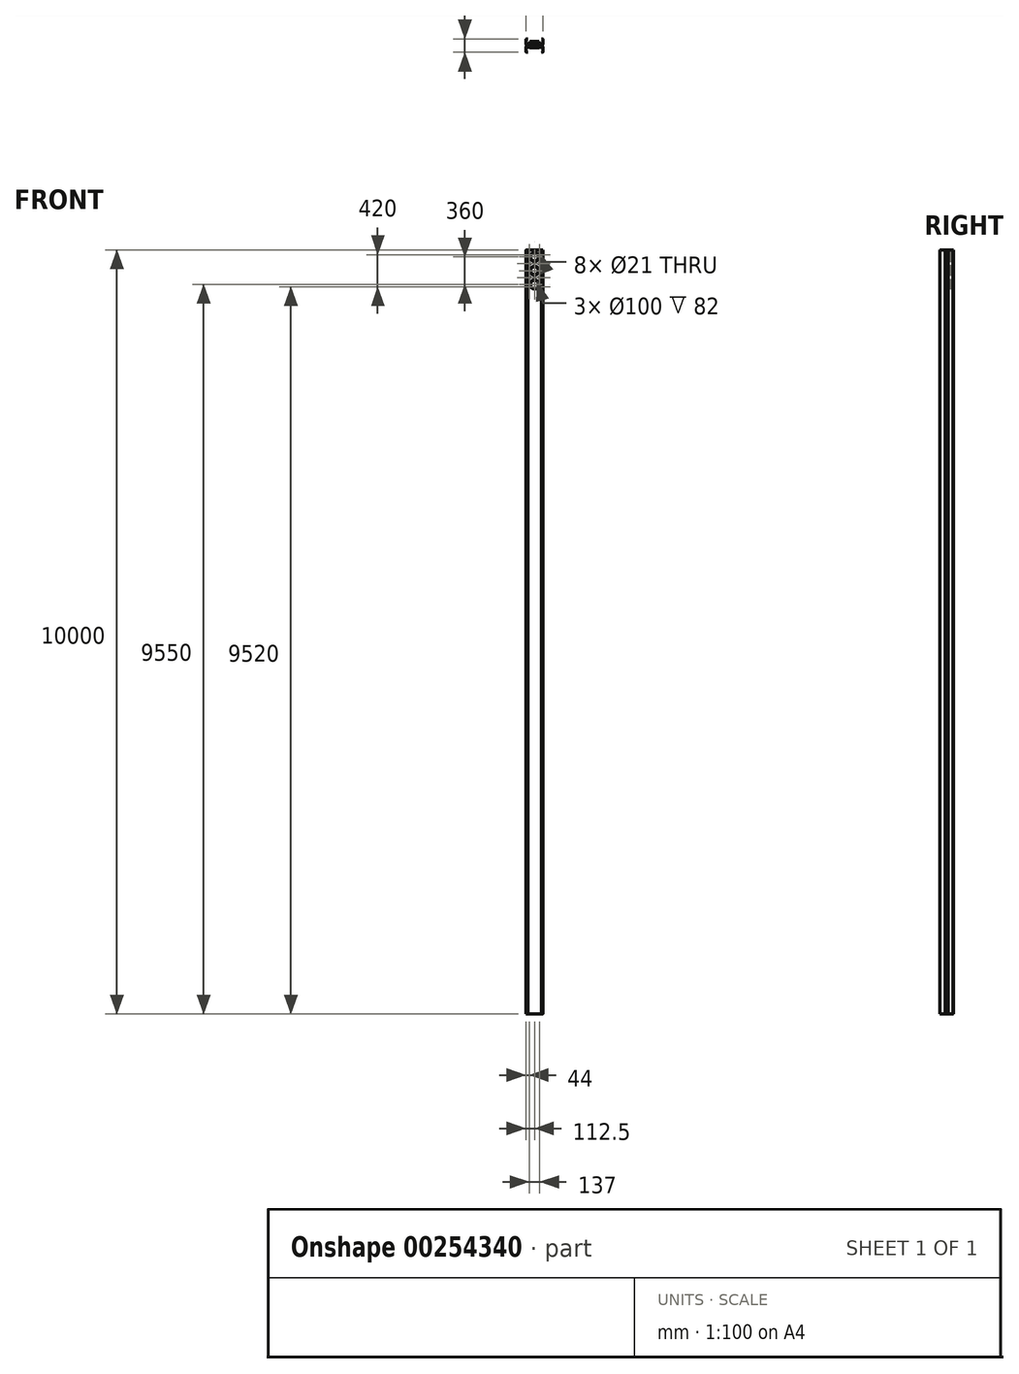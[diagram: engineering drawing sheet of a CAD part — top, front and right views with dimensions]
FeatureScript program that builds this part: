
annotation { "Feature Type Name" : "Feature", "Feature Type Description" : "" }
export const myFeature = defineFeature(function(context is Context, id is Id, definition is map)
    precondition{}
    {
        {
            var Q0;
            Q0=qCreatedBy(makeId("Top.planeOp"),FACE);
            var sketch = newSketch(context, id + "F0", { "sketchPlane" : qUnion([Q0])});
            skLineSegment(sketch, "E0.bottom", {"start": v(-107.5, 92.78) * mm, "end": v(-88.5, 92.78) * mm});
            skLineSegment(sketch, "E0.top", {"start": v(-107.5, -82.22) * mm, "end": v(-88.5, -82.22) * mm});
            skLineSegment(sketch, "E0.left", {"start": v(-112.5, 87.78) * mm, "end": v(-112.5, 26.84) * mm});
            skLineSegment(sketch, "E0.right", {"start": v(112.5, -18.27) * mm, "end": v(112.5, -77.22) * mm});
            skLineSegment(sketch, "E1.bottom", {"start": v(-104, 89.28) * mm, "end": v(-88.5, 89.28) * mm});
            skLineSegment(sketch, "E1.top", {"start": v(-104, 27.78) * mm, "end": v(104, 27.78) * mm});
            skLineSegment(sketch, "E1.left", {"start": v(-109, 84.28) * mm, "end": v(-109, 32.78) * mm});
            skLineSegment(sketch, "E1.right", {"start": v(109, 84.28) * mm, "end": v(109, 32.78) * mm});
            skLineSegment(sketch, "E2.bottom", {"start": v(-104, -17.22) * mm, "end": v(104, -17.22) * mm});
            skLineSegment(sketch, "E2.top", {"start": v(-104, -78.72) * mm, "end": v(-88.5, -78.72) * mm});
            skLineSegment(sketch, "E2.left", {"start": v(-109, -22.22) * mm, "end": v(-109, -73.72) * mm});
            skLineSegment(sketch, "E2.right", {"start": v(109, -22.22) * mm, "end": v(109, -73.72) * mm});
            skLineSegment(sketch, "E3.left", {"start": v(-88.5, 92.78) * mm, "end": v(-88.5, 89.28) * mm});
            skLineSegment(sketch, "E3.right", {"start": v(88.5, 92.78) * mm, "end": v(88.5, 89.28) * mm});
            skLineSegment(sketch, "E4.trimOffspring", {"start": v(-88.5, -78.72) * mm, "end": v(-88.5, -82.22) * mm});
            skLineSegment(sketch, "E5.trimOffspring", {"start": v(88.5, -78.72) * mm, "end": v(88.5, -82.22) * mm});
            skLineSegment(sketch, "E6.trimOffspring", {"start": v(88.5, -82.22) * mm, "end": v(107.5, -82.22) * mm});
            skLineSegment(sketch, "E7.trimOffspring", {"start": v(88.5, -78.72) * mm, "end": v(104, -78.72) * mm});
            skLineSegment(sketch, "E8.trimOffspring", {"start": v(88.5, 89.28) * mm, "end": v(104, 89.28) * mm});
            skLineSegment(sketch, "E9.trimOffspring", {"start": v(88.5, 92.78) * mm, "end": v(107.5, 92.78) * mm});
            skPoint(sketch, "E10.visualSharp", {"position": v(-109, 89.28) * mm});
            skArc(sketch, "E10.filletArc", {"start": v(-104, 89.28) * mm, "mid": v(-107.54, 87.81) * mm, "end": v(-109, 84.28) * mm});
            skPoint(sketch, "E11.visualSharp", {"position": v(109, 89.28) * mm});
            skArc(sketch, "E11.filletArc", {"start": v(109, 84.28) * mm, "mid": v(107.54, 87.81) * mm, "end": v(104, 89.28) * mm});
            skPoint(sketch, "E12.visualSharp", {"position": v(112.5, 92.78) * mm});
            skArc(sketch, "E12.filletArc", {"start": v(112.5, 87.78) * mm, "mid": v(111.04, 91.31) * mm, "end": v(107.5, 92.78) * mm});
            skArc(sketch, "E13.filletArc", {"start": v(-107.5, 92.78) * mm, "mid": v(-111.04, 91.31) * mm, "end": v(-112.5, 87.78) * mm});
            skPoint(sketch, "E14.visualSharp", {"position": v(-109, -78.72) * mm});
            skArc(sketch, "E14.filletArc", {"start": v(-109, -73.72) * mm, "mid": v(-107.54, -77.26) * mm, "end": v(-104, -78.72) * mm});
            skArc(sketch, "E15.filletArc", {"start": v(-112.38, -78.32) * mm, "mid": v(-110.62, -81.13) * mm, "end": v(-107.5, -82.22) * mm});
            skPoint(sketch, "E16.visualSharp", {"position": v(109, -78.72) * mm});
            skArc(sketch, "E16.filletArc", {"start": v(104, -78.72) * mm, "mid": v(107.54, -77.26) * mm, "end": v(109, -73.72) * mm});
            skArc(sketch, "E17.filletArc", {"start": v(107.5, -82.22) * mm, "mid": v(111.04, -80.76) * mm, "end": v(112.5, -77.22) * mm});
            skPoint(sketch, "E18.visualSharp", {"position": v(-109, 27.78) * mm});
            skArc(sketch, "E18.filletArc", {"start": v(-109, 32.78) * mm, "mid": v(-107.54, 29.24) * mm, "end": v(-104, 27.78) * mm});
            skPoint(sketch, "E19.visualSharp", {"position": v(109, 27.78) * mm});
            skArc(sketch, "E19.filletArc", {"start": v(104, 27.78) * mm, "mid": v(107.54, 29.24) * mm, "end": v(109, 32.78) * mm});
            skLineSegment(sketch, "E20", {"start": v(106.5, 27.78) * mm, "end": v(106.5, 21.6) * mm});
            skArc(sketch, "E21.filletArc", {"start": v(-112.5, 26.84) * mm, "mid": v(-111.04, 23.3) * mm, "end": v(-107.5, 21.84) * mm});
            skLineSegment(sketch, "E22", {"start": v(-112.38, -78.32) * mm, "end": v(-112.38, -18.42) * mm});
            skPoint(sketch, "E23.visualSharp", {"position": v(-109, -17.22) * mm});
            skArc(sketch, "E23.filletArc", {"start": v(-104, -17.22) * mm, "mid": v(-107.54, -18.69) * mm, "end": v(-109, -22.22) * mm});
            skPoint(sketch, "E24.visualSharp", {"position": v(-112.38, -22.95) * mm});
            skArc(sketch, "E24.filletArc", {"start": v(-107.5, -13.42) * mm, "mid": v(-110.96, -14.92) * mm, "end": v(-112.38, -18.42) * mm});
            skPoint(sketch, "E25.orphan", {"position": v(-106.5, -17.22) * mm});
            skLineSegment(sketch, "E26", {"start": v(-107.5, 21.84) * mm, "end": v(-107.5, -13.42) * mm});
            skLineSegment(sketch, "E27", {"start": v(106.5, 21.6) * mm, "end": v(106.76, 21.6) * mm});
            skLineSegment(sketch, "E28", {"start": v(106.5, -13.27) * mm, "end": v(107.5, -13.27) * mm});
            skPoint(sketch, "E29.visualSharp", {"position": v(109, -17.22) * mm});
            skArc(sketch, "E29.filletArc", {"start": v(109, -22.22) * mm, "mid": v(107.54, -18.69) * mm, "end": v(104, -17.22) * mm});
            skArc(sketch, "E30.filletArc", {"start": v(112.5, -18.27) * mm, "mid": v(111.04, -14.73) * mm, "end": v(107.5, -13.27) * mm});
            skLineSegment(sketch, "E31", {"start": v(112.5, 87.78) * mm, "end": v(111.76, 26.54) * mm});
            skArc(sketch, "E32.filletArc", {"start": v(106.76, 21.6) * mm, "mid": v(110.27, 23.04) * mm, "end": v(111.76, 26.54) * mm});
            skLineSegment(sketch, "E33", {"start": v(106.5, 21.6) * mm, "end": v(106.5, -13.27) * mm});
            skSolve(sketch);
        }
        {
            var Q0;
            Q0=makeQuery(id+"F0.imprint","IMPRINT",FACE,{"disambiguationData":[TD([[makeQuery(id+"F0.imprint","IMPRINT",EDGE,{"derivedFrom":sQuery(id+"F0.wireOp",EDGE,"E0.bottom")}),-1.0]])]});
            extrude(context, id + "F1", {"entities" : qUnion([Q0]), "flatOperationType" : FlatOperationType.REMOVE, "offsetDistance" : 25 * mm, "depth" : 10000 * mm, "domain" : OperationDomain.MODEL});
        }
        {
            var Q0;
            Q0=makeQuery(id+"F1.opExtrude","SWEPT_FACE",FACE,{"disambiguationData":[OSD([sQuery(id+"F0.wireOp",EDGE,"E2.bottom")])]});
            var sketch = newSketch(context, id + "F2", { "sketchPlane" : qUnion([Q0])});
            skCircle(sketch, "E34", {"center": v(0, 9910) * mm, "radius": 50 * mm});
            skPoint(sketch, "E34.centerSnap0", {"position": v(0, 10000) * mm});
            skCircle(sketch, "E35", {"center": v(0, 9730) * mm, "radius": 50 * mm});
            skCircle(sketch, "E36", {"center": v(0, 9550) * mm, "radius": 50 * mm});
            skCircle(sketch, "E37", {"center": v(-68.5, 9940) * mm, "radius": 10.5 * mm});
            skCircle(sketch, "E38", {"center": v(-68.5, 9820) * mm, "radius": 10.5 * mm});
            skCircle(sketch, "E39", {"center": v(-68.5, 9640) * mm, "radius": 10.5 * mm});
            skCircle(sketch, "E40", {"center": v(-68.5, 9520) * mm, "radius": 10.5 * mm});
            skCircle(sketch, "E41.1.0.0", {"center": v(68.5, 9940) * mm, "radius": 10.5 * mm});
            skCircle(sketch, "E41.1.0.1", {"center": v(68.5, 9640) * mm, "radius": 10.5 * mm});
            skCircle(sketch, "E41.1.0.2", {"center": v(68.5, 9520) * mm, "radius": 10.5 * mm});
            skCircle(sketch, "E41.1.0.3", {"center": v(68.5, 9820) * mm, "radius": 10.5 * mm});
            skLineSegment(sketch, "E41.direction1", {"start": v(-68.5, 9940) * mm, "end": v(68.5, 9940) * mm, "construction": true});
            skSolve(sketch);
        }
        {
            var Q0;
            Q0=makeQuery(id+"F2.imprint","IMPRINT",FACE,{"disambiguationData":[TD([[makeQuery(id+"F2.imprint","IMPRINT",EDGE,{"derivedFrom":sQuery(id+"F2.wireOp",EDGE,"E37")}),1.0]])]});
            var Q1;
            Q1=makeQuery(id+"F2.imprint","IMPRINT",FACE,{"disambiguationData":[TD([[makeQuery(id+"F2.imprint","IMPRINT",EDGE,{"derivedFrom":sQuery(id+"F2.wireOp",EDGE,"E38")}),1.0]])]});
            var Q2;
            Q2=makeQuery(id+"F2.imprint","IMPRINT",FACE,{"disambiguationData":[TD([[makeQuery(id+"F2.imprint","IMPRINT",EDGE,{"derivedFrom":sQuery(id+"F2.wireOp",EDGE,"E39")}),1.0]])]});
            var Q3;
            Q3=makeQuery(id+"F2.imprint","IMPRINT",FACE,{"disambiguationData":[TD([[makeQuery(id+"F2.imprint","IMPRINT",EDGE,{"derivedFrom":sQuery(id+"F2.wireOp",EDGE,"E40")}),1.0]])]});
            var Q4;
            Q4=makeQuery(id+"F2.imprint","IMPRINT",FACE,{"disambiguationData":[TD([[makeQuery(id+"F2.imprint","IMPRINT",EDGE,{"derivedFrom":sQuery(id+"F2.wireOp",EDGE,"E41.1.0.2")}),1.0]])]});
            var Q5;
            Q5=makeQuery(id+"F2.imprint","IMPRINT",FACE,{"disambiguationData":[TD([[makeQuery(id+"F2.imprint","IMPRINT",EDGE,{"derivedFrom":sQuery(id+"F2.wireOp",EDGE,"E41.1.0.1")}),1.0]])]});
            var Q6;
            Q6=makeQuery(id+"F2.imprint","IMPRINT",FACE,{"disambiguationData":[TD([[makeQuery(id+"F2.imprint","IMPRINT",EDGE,{"derivedFrom":sQuery(id+"F2.wireOp",EDGE,"E41.1.0.3")}),1.0]])]});
            var Q7;
            Q7=makeQuery(id+"F2.imprint","IMPRINT",FACE,{"disambiguationData":[TD([[makeQuery(id+"F2.imprint","IMPRINT",EDGE,{"derivedFrom":sQuery(id+"F2.wireOp",EDGE,"E41.1.0.0")}),1.0]])]});
            var Q8;
            Q8=makeQuery(id+"F2.imprint","IMPRINT",FACE,{"disambiguationData":[TD([[makeQuery(id+"F2.imprint","IMPRINT",EDGE,{"derivedFrom":sQuery(id+"F2.wireOp",EDGE,"E34")}),1.0]])]});
            var Q9;
            Q9=makeQuery(id+"F2.imprint","IMPRINT",FACE,{"disambiguationData":[TD([[makeQuery(id+"F2.imprint","IMPRINT",EDGE,{"derivedFrom":sQuery(id+"F2.wireOp",EDGE,"E35")}),1.0]])]});
            var Q10;
            Q10=makeQuery(id+"F2.imprint","IMPRINT",FACE,{"disambiguationData":[TD([[makeQuery(id+"F2.imprint","IMPRINT",EDGE,{"derivedFrom":sQuery(id+"F2.wireOp",EDGE,"E36")}),1.0]])]});
            extrude(context, id + "F3", {"entities" : qUnion([Q0, Q1, Q2, Q3, Q4, Q5, Q6, Q7, Q8, Q9, Q10]), "operationType" : NewBodyOperationType.REMOVE, "endBound" : BoundingType.THROUGH_ALL, "oppositeDirection" : true, "depth" : 25 * mm});
        }
        {
            var Q0;
            Q0=makeQuery(id+"F1.opExtrude","SWEPT_FACE",FACE,{"disambiguationData":[OSD([sQuery(id+"F0.wireOp",EDGE,"E2.bottom")])]});
            var sketch = newSketch(context, id + "F4", { "sketchPlane" : qUnion([Q0])});
            skCircle(sketch, "E42", {"center": v(0, 9910) * mm, "radius": 60 * mm});
            skCircle(sketch, "E43.0.1.0", {"center": v(0, 9730) * mm, "radius": 60 * mm});
            skCircle(sketch, "E43.0.2.0", {"center": v(0, 9550) * mm, "radius": 60 * mm});
            skLineSegment(sketch, "E43.direction1", {"start": v(0, 9910) * mm, "end": v(25, 9910) * mm, "construction": true});
            skLineSegment(sketch, "E43.direction2", {"start": v(0, 9910) * mm, "end": v(0, 9730) * mm, "construction": true});
            skSolve(sketch);
        }
        {
            var Q0;
            Q0=makeQuery(id+"F4.imprint","IMPRINT",FACE,{"disambiguationData":[TD([[makeQuery(id+"F4.imprint","IMPRINT",EDGE,{"derivedFrom":sQuery(id+"F4.wireOp",EDGE,"E43.0.2.0")}),1.0]])]});
            var Q1;
            Q1=makeQuery(id+"F4.imprint","IMPRINT",FACE,{"disambiguationData":[TD([[makeQuery(id+"F4.imprint","IMPRINT",EDGE,{"derivedFrom":sQuery(id+"F4.wireOp",EDGE,"E42")}),1.0]])]});
            var Q2;
            Q2=makeQuery(id+"F4.imprint","IMPRINT",FACE,{"disambiguationData":[TD([[makeQuery(id+"F4.imprint","IMPRINT",EDGE,{"derivedFrom":sQuery(id+"F4.wireOp",EDGE,"E43.0.1.0")}),1.0]])]});
            extrude(context, id + "F5", {"entities" : qUnion([Q0, Q1, Q2]), "operationType" : NewBodyOperationType.ADD, "depth" : 5 * mm});
        }
        {
            var Q0;
            Q0=makeQuery(id+"F5.opExtrude","CAP_FACE",FACE,{"disambiguationData":[OSD([sQuery(id+"F2.wireOp",EDGE,"E35"),sQuery(id+"F4.wireOp",EDGE,"E43.0.1.0")])],"isStart":false});
            var Q1;
            Q1=makeQuery(id+"F5.opExtrude","CAP_FACE",FACE,{"disambiguationData":[OSD([sQuery(id+"F2.wireOp",EDGE,"E34"),sQuery(id+"F4.wireOp",EDGE,"E42")])],"isStart":false});
            var Q2;
            Q2=makeQuery(id+"F5.opExtrude","CAP_FACE",FACE,{"disambiguationData":[OSD([sQuery(id+"F2.wireOp",EDGE,"E36"),sQuery(id+"F4.wireOp",EDGE,"E43.0.2.0")])],"isStart":false});
            extrude(context, id + "F6", {"entities" : qUnion([Q0, Q1, Q2]), "operationType" : NewBodyOperationType.ADD, "oppositeDirection" : true, "depth" : 82 * mm});
        }
    });
